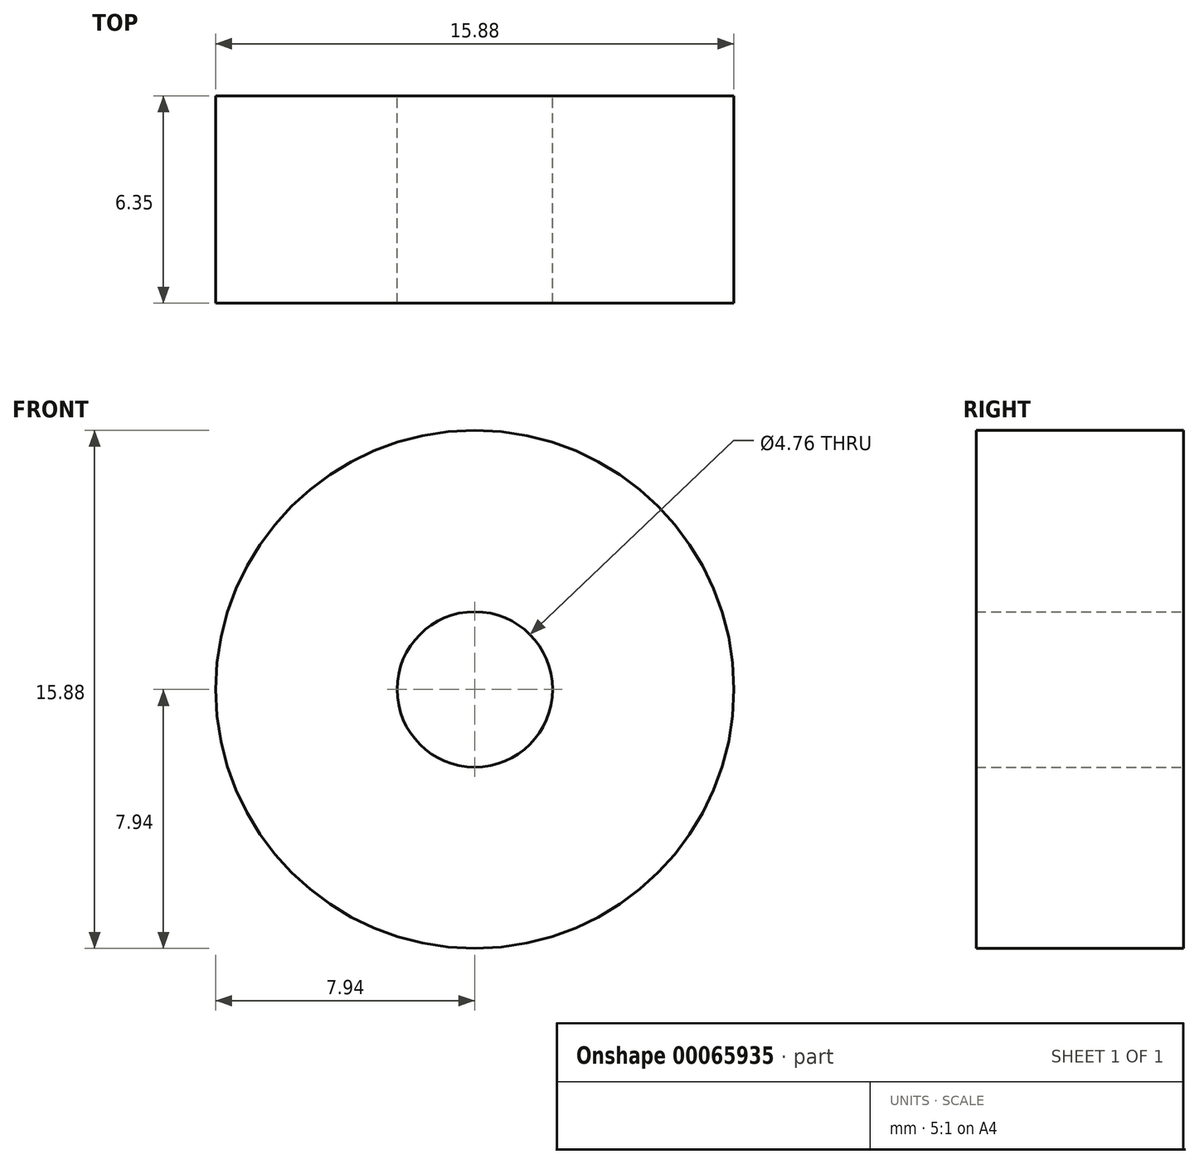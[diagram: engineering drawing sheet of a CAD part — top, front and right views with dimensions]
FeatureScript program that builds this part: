
annotation { "Feature Type Name" : "Feature", "Feature Type Description" : "" }
export const myFeature = defineFeature(function(context is Context, id is Id, definition is map)
    precondition{}
    {
        {
            var Q0;
            Q0=qCreatedBy(makeId("Front.planeOp"),FACE);
            var sketch = newSketch(context, id + "F0", { "sketchPlane" : qUnion([Q0])});
            skCircle(sketch, "E0", {"center": v(0, 0) * mm, "radius": 7.94 * mm});
            skCircle(sketch, "E1", {"center": v(0, 0) * mm, "radius": 2.38 * mm});
            skSolve(sketch);
        }
        {
            var Q0;
            Q0 = qSketchRegion(id + "F0", true);
            extrude(context, id + "F1", {"entities" : qUnion([Q0]), "depth" : 6.35 * mm});
        }
    });
